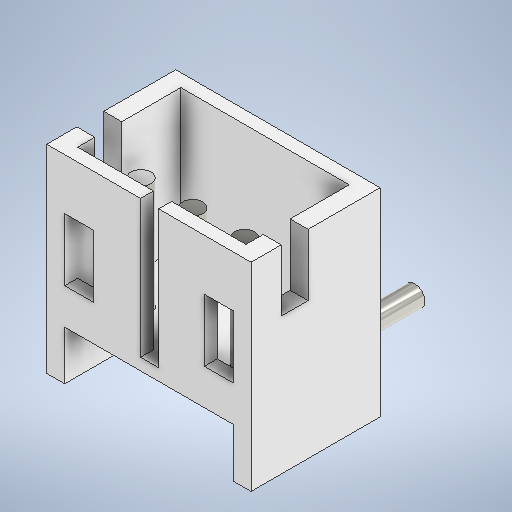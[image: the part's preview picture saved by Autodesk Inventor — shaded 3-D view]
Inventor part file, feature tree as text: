
AUTODESK INVENTOR PART (.ipt)
format: ipt  version: 2025 (Build 290162000, 162)  size: 349,696 bytes
history: native  units: in
note: dims shown in document units (in); Inventor stores cm internally (conversion verified against a paired STEP export)
features: sketch x8, extrude x6, plane x1, sweep x1
ambient origin geometry x8: Origin, YZ Plane, XZ Plane, XY Plane, X Axis, Y Axis, Z Axis, Center Point
bodies: Solid1 (feature_tree)
feature tree (16):
  extrude  "Extrusion1"  Depth=0.312in
  extrude  "Extrusion3"  Depth=0.197in
  extrude  "Extrusion4"  Depth=0.075in TaperAngle=0.0deg
  extrude  "Extrusion7"  Depth=0.0439in
  sketch  "Sketch10"  dims[d38=1.0in d39=0.0in d40=0.067in]
  plane  "Work Plane1"
  sweep  "Sweep1"
  extrude  "Extrusion8"  Depth=0.1285in
  extrude  "Extrusion9"  Depth=0.067in
  sketch  "Sketch1"  dims[d0=0.303in d1=0.312in]
  sketch  "Sketch4"  dims[d2=0.197in d3=0.0in d16=0.0985in]
  sketch  "Sketch5"  dims[d17=0.21in d18=0.0in d19=0.075in d20=0.0in]
  sketch  "Sketch9"  dims[d36=0.0439in d37=0.0439in]
  sketch  "Sketch11"  dims[d41=0.031in d42=0.1285in]
  sketch  "Sketch12"  dims[d43=0.031in d44=0.067in]
  sketch  "Sketch13"  dims[d45=0.079in d46=0.031in d47=0.067in d48=0.079in d49=0.0394in d50=0.13in d51=0.246in d52=0.02in d53=0.0in d54=0.0in d55=1.0in d56=0.0in d57=1.0in d58=0.0in]
